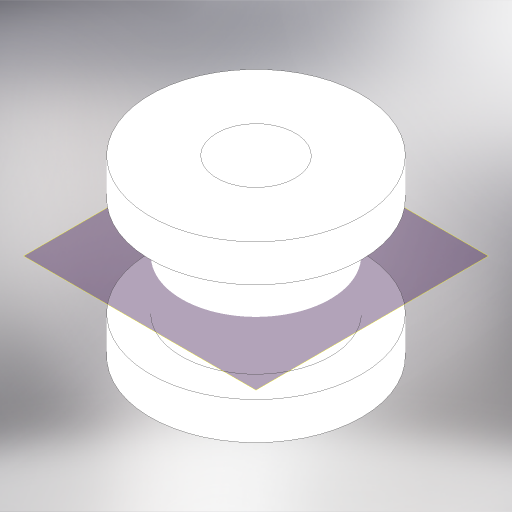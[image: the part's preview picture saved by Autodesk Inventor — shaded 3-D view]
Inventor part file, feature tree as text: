
AUTODESK INVENTOR PART (.ipt)
format: ipt  version: 2023 (Build 270158000, 158)  size: 249,344 bytes
history: native  units: mm
features: extrude x2, plane x2, sketch x2, mirror x1
ambient origin geometry x8: Origin, YZ Plane, XZ Plane, XY Plane, X Axis, Y Axis, Z Axis, Center Point
bodies: Solid1 (feature_tree)
feature tree (7):
  extrude  "Extrusion1"  Depth=12.0mm
  extrude  "Extrusion2"  Depth=3.0mm
  plane  "Work Plane1"
  mirror  "Mirror1"
  sketch  "Sketch1"  dims[d0=6.3mm d2=12.0mm]
  sketch  "Sketch2"  dims[d3=11.0mm d4=0.0mm d5=17.0mm d6=3.0mm d7=0.0mm]
  plane  "Work Plane2"
